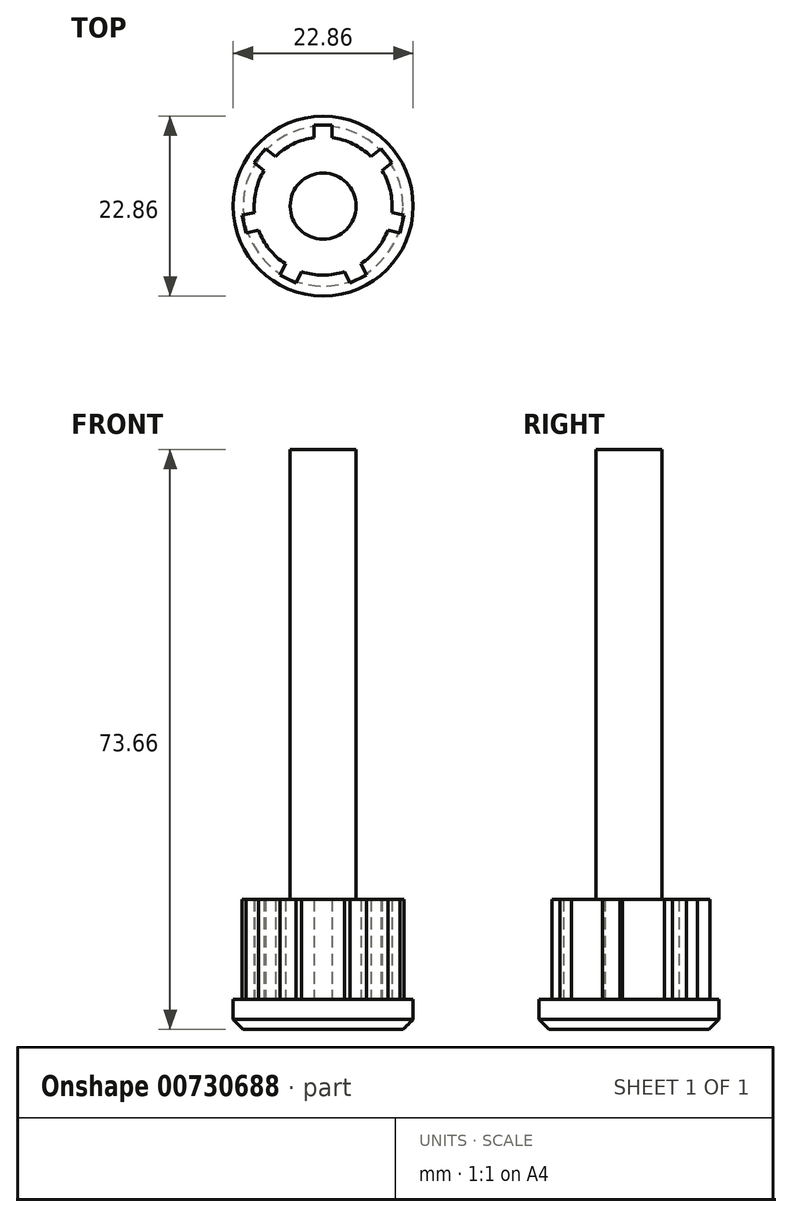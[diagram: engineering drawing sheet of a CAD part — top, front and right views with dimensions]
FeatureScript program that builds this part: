
annotation { "Feature Type Name" : "Feature", "Feature Type Description" : "" }
export const myFeature = defineFeature(function(context is Context, id is Id, definition is map)
    precondition{}
    {
        {
            var Q0;
            Q0=qCreatedBy(makeId("Top.planeOp"),FACE);
            var sketch = newSketch(context, id + "F0", { "sketchPlane" : qUnion([Q0])});
            skCircle(sketch, "E0", {"center": v(0, 0) * mm, "radius": 11.43 * mm});
            skSolve(sketch);
        }
        {
            var Q0;
            Q0 = qSketchRegion(id + "F0", true);
            extrude(context, id + "F1", {"entities" : qUnion([Q0]), "depth" : 3.8 * mm, "offsetDistance" : 25.4 * mm});
        }
        {
            var Q0;
            Q0=makeQuery(id+"F1.opExtrude","CAP_FACE",FACE,{"disambiguationData":[OSD([sQuery(id+"F0.wireOp",EDGE,"E0")])],"isStart":false});
            var sketch = newSketch(context, id + "F2", { "sketchPlane" : qUnion([Q0])});
            skCircle(sketch, "E1", {"center": v(0, 0) * mm, "radius": 8.76 * mm});
            skLineSegment(sketch, "E2", {"start": v(-1.14, 8.69) * mm, "end": v(-1.14, 10.29) * mm});
            skLineSegment(sketch, "E3", {"start": v(-1.14, 10.29) * mm, "end": v(1.14, 10.29) * mm});
            skLineSegment(sketch, "E4", {"start": v(1.14, 10.29) * mm, "end": v(1.14, 8.69) * mm});
            skLineSegment(sketch, "E5.1.0", {"start": v(-7.33, 7.3) * mm, "end": v(-6.08, 6.31) * mm});
            skLineSegment(sketch, "E5.1.1", {"start": v(-8.76, 5.52) * mm, "end": v(-7.33, 7.3) * mm});
            skLineSegment(sketch, "E5.1.2", {"start": v(-7.5, 4.52) * mm, "end": v(-8.76, 5.52) * mm});
            skLineSegment(sketch, "E5.2.0", {"start": v(-10.28, -1.17) * mm, "end": v(-8.72, -0.82) * mm});
            skLineSegment(sketch, "E5.2.1", {"start": v(-9.77, -3.4) * mm, "end": v(-10.28, -1.17) * mm});
            skLineSegment(sketch, "E5.2.2", {"start": v(-8.22, -3.05) * mm, "end": v(-9.77, -3.4) * mm});
            skLineSegment(sketch, "E5.3.0", {"start": v(-5.5, -8.77) * mm, "end": v(-4.8, -7.33) * mm});
            skLineSegment(sketch, "E5.3.1", {"start": v(-3.43, -9.76) * mm, "end": v(-5.5, -8.77) * mm});
            skLineSegment(sketch, "E5.3.2", {"start": v(-2.74, -8.32) * mm, "end": v(-3.43, -9.76) * mm});
            skLineSegment(sketch, "E5.4.0", {"start": v(3.43, -9.76) * mm, "end": v(2.74, -8.32) * mm});
            skLineSegment(sketch, "E5.4.1", {"start": v(5.5, -8.77) * mm, "end": v(3.43, -9.76) * mm});
            skLineSegment(sketch, "E5.4.2", {"start": v(4.8, -7.33) * mm, "end": v(5.5, -8.77) * mm});
            skLineSegment(sketch, "E5.5.0", {"start": v(9.77, -3.4) * mm, "end": v(8.22, -3.05) * mm});
            skLineSegment(sketch, "E5.5.1", {"start": v(10.28, -1.17) * mm, "end": v(9.77, -3.4) * mm});
            skLineSegment(sketch, "E5.5.2", {"start": v(8.72, -0.82) * mm, "end": v(10.28, -1.17) * mm});
            skLineSegment(sketch, "E5.6.0", {"start": v(8.76, 5.52) * mm, "end": v(7.5, 4.52) * mm});
            skLineSegment(sketch, "E5.6.1", {"start": v(7.33, 7.3) * mm, "end": v(8.76, 5.52) * mm});
            skLineSegment(sketch, "E5.6.2", {"start": v(6.08, 6.31) * mm, "end": v(7.33, 7.3) * mm});
            skSolve(sketch);
        }
        {
            var Q0;
            {var subQ1=sQuery(id+"F2.wireOp",EDGE,"E1");var subQ12=sQuery(id+"F2.wireOp",EDGE,"e3c732c1-35c0-4129-a19f-95bca32be8e5.6.0");var subQ13=makeQuery(id+"F2.imprint","INTERSECT",VERTEX,{"disambiguationData":[OD(0.0)],"derivedFrom":[subQ1,subQ12]});Q0=makeQuery(id+"F2.imprint","IMPRINT",FACE,{"disambiguationData":[TD([[makeQuery(id+"F2.imprint","IMPRINT",EDGE,{"disambiguationData":[TD([[subQ13,-1.0]])],"derivedFrom":subQ1}),1.0]])]});}
            var Q1;
            {var subQ0=sQuery(id+"F2.wireOp",EDGE,"e3c732c1-35c0-4129-a19f-95bca32be8e5.1.0");Q1=makeQuery(id+"F2.imprint","IMPRINT",FACE,{"disambiguationData":[TD([[makeQuery(id+"F2.imprint","IMPRINT",EDGE,{"derivedFrom":subQ0}),1.0]])]});}
            var Q2;
            {var subQ0=sQuery(id+"F2.wireOp",EDGE,"e3c732c1-35c0-4129-a19f-95bca32be8e5.2.0");Q2=makeQuery(id+"F2.imprint","IMPRINT",FACE,{"disambiguationData":[TD([[makeQuery(id+"F2.imprint","IMPRINT",EDGE,{"derivedFrom":subQ0}),1.0]])]});}
            var Q3;
            {var subQ0=sQuery(id+"F2.wireOp",EDGE,"e3c732c1-35c0-4129-a19f-95bca32be8e5.3.0");Q3=makeQuery(id+"F2.imprint","IMPRINT",FACE,{"disambiguationData":[TD([[makeQuery(id+"F2.imprint","IMPRINT",EDGE,{"derivedFrom":subQ0}),1.0]])]});}
            var Q4;
            {var subQ0=sQuery(id+"F2.wireOp",EDGE,"e3c732c1-35c0-4129-a19f-95bca32be8e5.4.0");Q4=makeQuery(id+"F2.imprint","IMPRINT",FACE,{"disambiguationData":[TD([[makeQuery(id+"F2.imprint","IMPRINT",EDGE,{"derivedFrom":subQ0}),1.0]])]});}
            var Q5;
            {var subQ0=sQuery(id+"F2.wireOp",EDGE,"e3c732c1-35c0-4129-a19f-95bca32be8e5.5.0");Q5=makeQuery(id+"F2.imprint","IMPRINT",FACE,{"disambiguationData":[TD([[makeQuery(id+"F2.imprint","IMPRINT",EDGE,{"derivedFrom":subQ0}),1.0]])]});}
            var Q6;
            {var subQ0=sQuery(id+"F2.wireOp",EDGE,"e3c732c1-35c0-4129-a19f-95bca32be8e5.6.0");Q6=makeQuery(id+"F2.imprint","IMPRINT",FACE,{"disambiguationData":[TD([[makeQuery(id+"F2.imprint","IMPRINT",EDGE,{"derivedFrom":subQ0}),1.0]])]});}
            var Q7;
            {var subQ0=sQuery(id+"F2.wireOp",EDGE,"TDlERv0R-6VSS-Pr0s-IU3l-JfIiLJ9VeMvw");Q7=makeQuery(id+"F2.imprint","IMPRINT",FACE,{"disambiguationData":[TD([[makeQuery(id+"F2.imprint","IMPRINT",EDGE,{"derivedFrom":subQ0}),1.0]])]});}
            extrude(context, id + "F3", {"entities" : qUnion([Q0, Q1, Q2, Q3, Q4, Q5, Q6, Q7]), "operationType" : NewBodyOperationType.ADD, "depth" : 12.7 * mm, "offsetDistance" : 25.4 * mm});
        }
        {
            var Q0;
            Q0=makeQuery(id+"F3.opExtrude","CAP_FACE",FACE,{"disambiguationData":[OSD([sQuery(id+"F2.wireOp",EDGE,"E1"),sQuery(id+"F2.wireOp",EDGE,"TDlERv0R-6VSS-Pr0s-IU3l-JfIiLJ9VeMvw"),sQuery(id+"F2.wireOp",EDGE,"e3c732c1-35c0-4129-a19f-95bca32be8e5.1.0"),sQuery(id+"F2.wireOp",EDGE,"e3c732c1-35c0-4129-a19f-95bca32be8e5.2.0"),sQuery(id+"F2.wireOp",EDGE,"e3c732c1-35c0-4129-a19f-95bca32be8e5.3.0"),sQuery(id+"F2.wireOp",EDGE,"e3c732c1-35c0-4129-a19f-95bca32be8e5.4.0"),sQuery(id+"F2.wireOp",EDGE,"e3c732c1-35c0-4129-a19f-95bca32be8e5.5.0"),sQuery(id+"F2.wireOp",EDGE,"e3c732c1-35c0-4129-a19f-95bca32be8e5.6.0")])],"isStart":false});
            var sketch = newSketch(context, id + "F4", { "sketchPlane" : qUnion([Q0])});
            skCircle(sketch, "E6", {"center": v(0, 0) * mm, "radius": 4.2 * mm});
            skSolve(sketch);
        }
        {
            var Q0;
            Q0 = qSketchRegion(id + "F4", true);
            extrude(context, id + "F5", {"entities" : qUnion([Q0]), "operationType" : NewBodyOperationType.ADD, "depth" : 57.15 * mm, "offsetDistance" : 25.4 * mm});
        }
        {
            var Q0;
            Q0 = qSketchRegion(id + "F4", true);
            extrude(context, id + "F6", {"entities" : qUnion([Q0]), "operationType" : NewBodyOperationType.ADD, "depth" : 57.15 * mm, "offsetDistance" : 25.4 * mm});
        }
        {
            var Q0;
            Q0=makeQuery(id+"F1.opExtrude","CAP_FACE",FACE,{"disambiguationData":[OSD([sQuery(id+"F0.wireOp",EDGE,"E0")])],"isStart":true});
            chamfer(context, id + "F7", {"entities" : qUnion([Q0]), "width" : 1.27 * mm, "tangentPropagation" : true});
        }
        {
            var Q0;
            Q0 = qSketchRegion(id + "F2", true);
            extrude(context, id + "F8", {"entities" : qUnion([Q0]), "operationType" : NewBodyOperationType.ADD, "depth" : 12.7 * mm, "offsetDistance" : 25.4 * mm});
        }
    });
